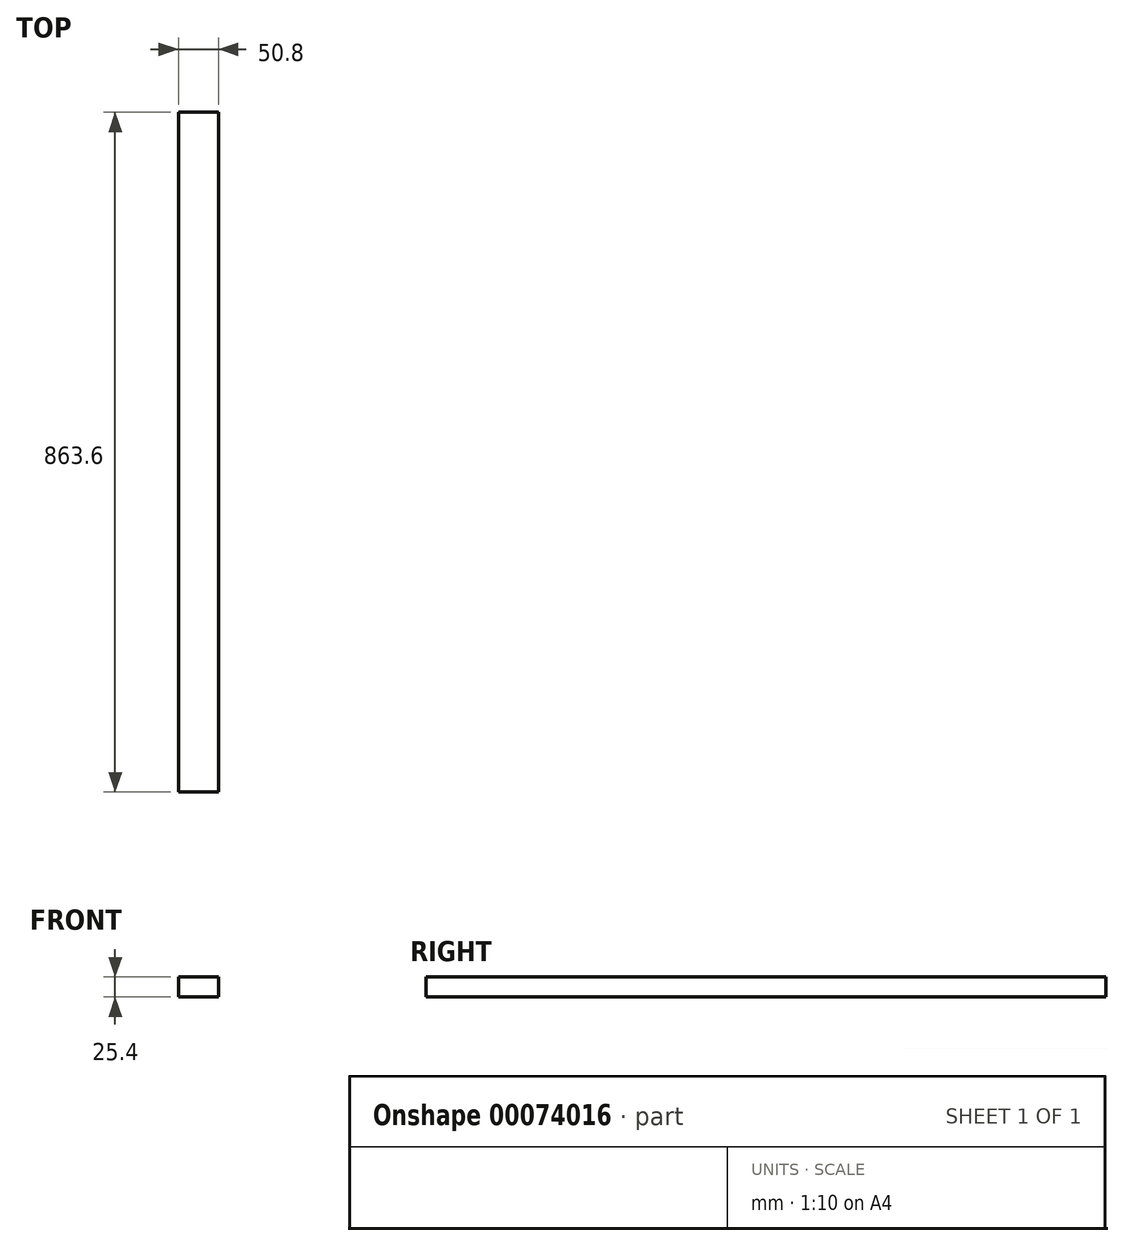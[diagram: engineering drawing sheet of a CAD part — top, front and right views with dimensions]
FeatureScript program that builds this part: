
annotation { "Feature Type Name" : "Feature", "Feature Type Description" : "" }
export const myFeature = defineFeature(function(context is Context, id is Id, definition is map)
    precondition{}
    {
        {
            var Q0;
            Q0=qCreatedBy(makeId("Right.planeOp"),FACE);
            var sketch = newSketch(context, id + "F0", { "sketchPlane" : qUnion([Q0])});
            skLineSegment(sketch, "E0.rect.bottom", {"start": v(-431.8, 12.7) * mm, "end": v(431.8, 12.7) * mm});
            skLineSegment(sketch, "E0.rect.top", {"start": v(-431.8, -12.7) * mm, "end": v(431.8, -12.7) * mm});
            skLineSegment(sketch, "E0.rect.left", {"start": v(-431.8, 12.7) * mm, "end": v(-431.8, -12.7) * mm});
            skLineSegment(sketch, "E0.rect.right", {"start": v(431.8, 12.7) * mm, "end": v(431.8, -12.7) * mm});
            skPoint(sketch, "E0.rect.middle", {"position": v(0, 0) * mm});
            skSolve(sketch);
        }
        {
            var Q0;
            Q0 = qSketchRegion(id + "F0", true);
            extrude(context, id + "F1", {"entities" : qUnion([Q0]), "depth" : 50.8 * mm});
        }
    });
